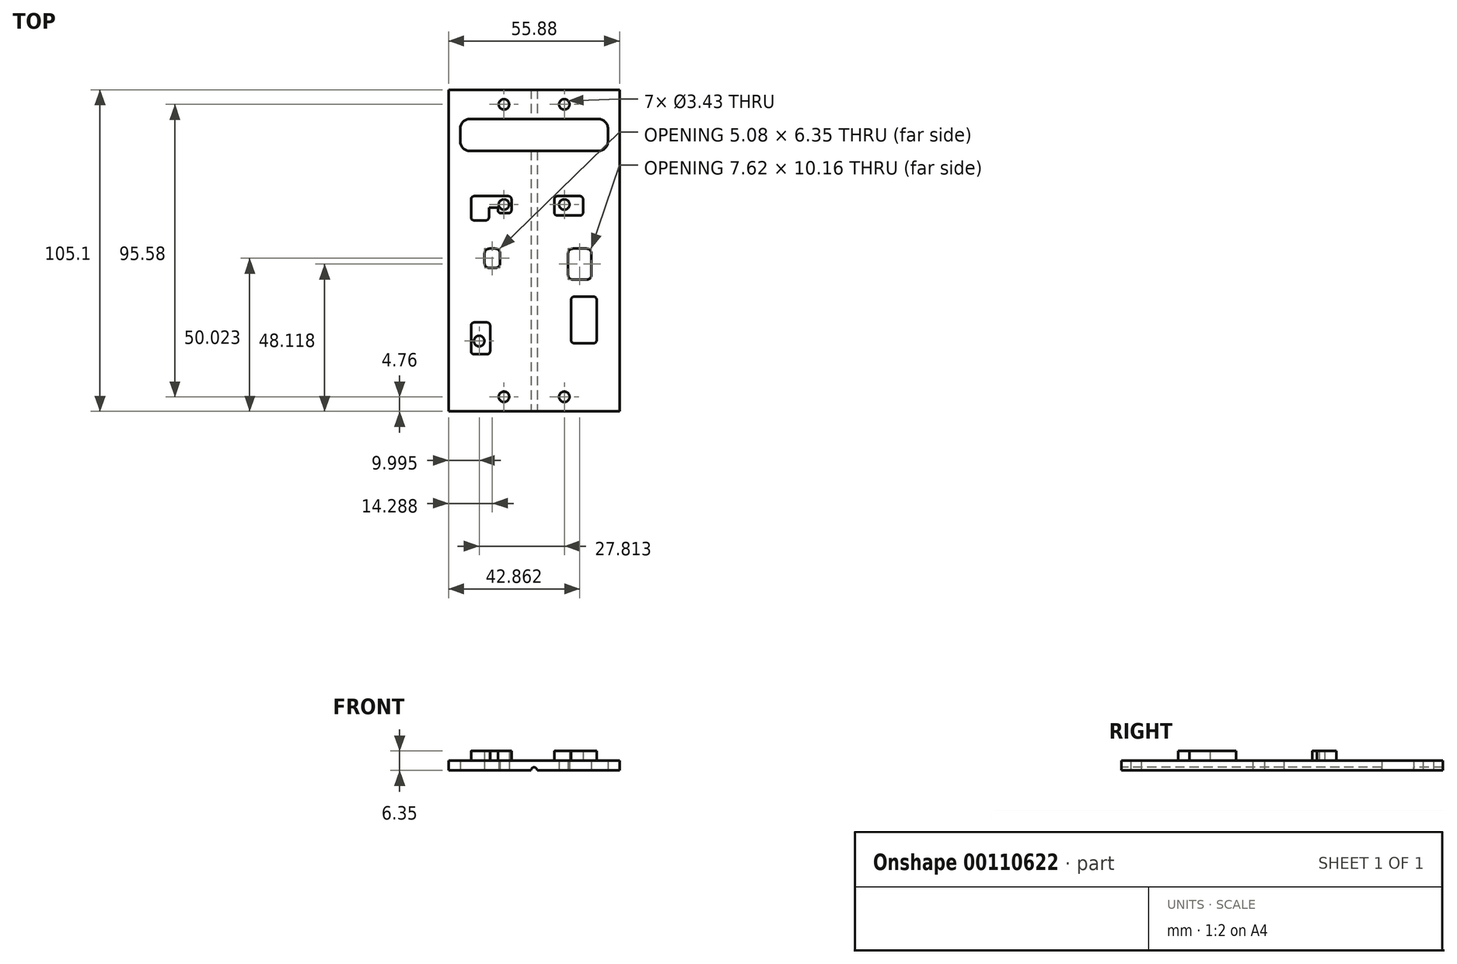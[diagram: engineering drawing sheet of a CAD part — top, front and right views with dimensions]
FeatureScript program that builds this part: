
annotation { "Feature Type Name" : "Feature", "Feature Type Description" : "" }
export const myFeature = defineFeature(function(context is Context, id is Id, definition is map)
    precondition{}
    {
        {
            var Q0;
            Q0=qCreatedBy(makeId("Top.planeOp"),FACE);
            var sketch = newSketch(context, id + "F0", { "sketchPlane" : qUnion([Q0])});
            skLineSegment(sketch, "E0.rect.bottom", {"start": v(27.94, 52.55) * mm, "end": v(-27.94, 52.55) * mm});
            skLineSegment(sketch, "E0.rect.top", {"start": v(27.94, -52.55) * mm, "end": v(-27.94, -52.55) * mm});
            skLineSegment(sketch, "E0.rect.left", {"start": v(27.94, 52.55) * mm, "end": v(27.94, -52.55) * mm});
            skLineSegment(sketch, "E0.rect.right", {"start": v(-27.94, 52.55) * mm, "end": v(-27.94, -52.55) * mm});
            skPoint(sketch, "E0.rect.middle", {"position": v(0, 0) * mm});
            skLineSegment(sketch, "E1.rect.bottom", {"start": v(24.13, 43.03) * mm, "end": v(-24.13, 43.03) * mm});
            skLineSegment(sketch, "E1.rect.top", {"start": v(24.13, 32.54) * mm, "end": v(-24.13, 32.54) * mm});
            skLineSegment(sketch, "E1.rect.left", {"start": v(24.13, 43.03) * mm, "end": v(24.13, 32.54) * mm});
            skLineSegment(sketch, "E1.rect.right", {"start": v(-24.13, 43.03) * mm, "end": v(-24.13, 32.54) * mm});
            skPoint(sketch, "E1.rect.middle", {"position": v(0, 37.78) * mm});
            skCircle(sketch, "E2", {"center": v(-9.87, 15.06) * mm, "radius": 1.71 * mm});
            skCircle(sketch, "E3", {"center": v(9.87, 15.06) * mm, "radius": 1.71 * mm});
            skLineSegment(sketch, "E4", {"start": v(-12.7, 29.36) * mm, "end": v(12.7, 29.36) * mm, "construction": true});
            skPoint(sketch, "E5", {"position": v(0, 29.36) * mm});
            skCircle(sketch, "E6", {"center": v(-9.87, 47.8) * mm, "radius": 1.71 * mm});
            skCircle(sketch, "E7", {"center": v(9.87, 47.8) * mm, "radius": 1.71 * mm});
            skLineSegment(sketch, "E8", {"start": v(0, 43.03) * mm, "end": v(0, 52.55) * mm, "construction": true});
            skPoint(sketch, "E9", {"position": v(0, 47.8) * mm});
            skCircle(sketch, "E10", {"center": v(-17.95, -29.57) * mm, "radius": 1.71 * mm});
            skLineSegment(sketch, "E11", {"start": v(-9.87, 15.06) * mm, "end": v(9.87, 15.06) * mm, "construction": true});
            skPoint(sketch, "E12", {"position": v(0, 15.06) * mm});
            skLineSegment(sketch, "E13", {"start": v(-27.94, -43.03) * mm, "end": v(27.94, -43.03) * mm, "construction": true});
            skCircle(sketch, "E14", {"center": v(-9.87, -47.8) * mm, "radius": 1.71 * mm});
            skCircle(sketch, "E15", {"center": v(9.87, -47.8) * mm, "radius": 1.71 * mm});
            skLineSegment(sketch, "E16", {"start": v(-9.87, -43.03) * mm, "end": v(-9.87, -52.55) * mm, "construction": true});
            skSolve(sketch);
        }
        {
            var Q0;
            Q0=qSketchRegion(id+"F0",true);
            extrude(context, id + "F1", {"entities" : qUnion([Q0]), "depth" : 3.17 * mm});
        }
        {
            var Q0;
            Q0=makeQuery(id+"F1.opExtrude","SWEPT_FACE",FACE,{"disambiguationData":[OSD([sQuery(id+"F0.wireOp",EDGE,"E0.rect.top")])]});
            var sketch = newSketch(context, id + "F2", { "sketchPlane" : qUnion([Q0])});
            skCircle(sketch, "E17", {"center": v(0, 0) * mm, "radius": 1.02 * mm});
            skSolve(sketch);
        }
        {
            var Q0;
            Q0=qSketchRegion(id+"F2",true);
            extrude(context, id + "F3", {"entities" : qUnion([Q0]), "operationType" : NewBodyOperationType.REMOVE, "endBound" : BoundingType.THROUGH_ALL, "oppositeDirection" : true, "depth" : 25.4 * mm});
        }
        {
            var Q0;
            Q0=makeQuery(id+"F1.opExtrude","CAP_FACE",FACE,{"disambiguationData":[OSD([sQuery(id+"F0.wireOp",EDGE,"E0.rect.bottom"),sQuery(id+"F0.wireOp",EDGE,"E0.rect.top"),sQuery(id+"F0.wireOp",EDGE,"E0.rect.left"),sQuery(id+"F0.wireOp",EDGE,"E0.rect.right"),sQuery(id+"F0.wireOp",EDGE,"E1.rect.bottom"),sQuery(id+"F0.wireOp",EDGE,"E1.rect.top"),sQuery(id+"F0.wireOp",EDGE,"E1.rect.left"),sQuery(id+"F0.wireOp",EDGE,"E1.rect.right"),sQuery(id+"F0.wireOp",EDGE,"E2"),sQuery(id+"F0.wireOp",EDGE,"E3"),sQuery(id+"F0.wireOp",EDGE,"E6"),sQuery(id+"F0.wireOp",EDGE,"E7"),sQuery(id+"F0.wireOp",EDGE,"E10"),sQuery(id+"F0.wireOp",EDGE,"a1c96030-42fa-4948-bc88-0ccc6f73de77")])],"isStart":false});
            var sketch = newSketch(context, id + "F4", { "sketchPlane" : qUnion([Q0])});
            skCircle(sketch, "E18", {"center": v(-17.95, -29.57) * mm, "radius": 1.71 * mm});
            skCircle(sketch, "E19", {"center": v(-9.87, 15.06) * mm, "radius": 1.71 * mm});
            skCircle(sketch, "E20", {"center": v(9.87, 15.06) * mm, "radius": 1.71 * mm});
            skLineSegment(sketch, "E21.bottom", {"start": v(20.45, 17.8) * mm, "end": v(-20.6, 17.8) * mm, "construction": true});
            skLineSegment(sketch, "E21.top", {"start": v(20.45, -33.9) * mm, "end": v(-20.6, -33.9) * mm, "construction": true});
            skLineSegment(sketch, "E21.left", {"start": v(20.45, 17.8) * mm, "end": v(20.45, -33.9) * mm, "construction": true});
            skLineSegment(sketch, "E21.right", {"start": v(-20.6, 17.8) * mm, "end": v(-20.6, -33.9) * mm, "construction": true});
            skLineSegment(sketch, "E22.bottom", {"start": v(-20.6, 17.8) * mm, "end": v(-7.4, 17.8) * mm});
            skLineSegment(sketch, "E22.left", {"start": v(-20.6, 17.8) * mm, "end": v(-20.6, 14.8) * mm});
            skLineSegment(sketch, "E22.right", {"start": v(-7.4, 17.8) * mm, "end": v(-7.4, 13.98) * mm});
            skLineSegment(sketch, "E23", {"start": v(-11.84, 13.98) * mm, "end": v(-14.76, 13.98) * mm});
            skLineSegment(sketch, "E24", {"start": v(-14.76, 13.98) * mm, "end": v(-14.76, 9.87) * mm});
            skLineSegment(sketch, "E25", {"start": v(-14.76, 9.87) * mm, "end": v(-20.6, 9.87) * mm});
            skLineSegment(sketch, "E26", {"start": v(-20.6, 9.87) * mm, "end": v(-20.6, 14.8) * mm});
            skLineSegment(sketch, "E27", {"start": v(-7.4, 13.98) * mm, "end": v(-7.4, 12.2) * mm});
            skLineSegment(sketch, "E28", {"start": v(-7.4, 12.2) * mm, "end": v(-11.84, 12.2) * mm});
            skLineSegment(sketch, "E29", {"start": v(-11.84, 12.2) * mm, "end": v(-11.84, 13.98) * mm});
            skLineSegment(sketch, "E30.bottom", {"start": v(16, 17.8) * mm, "end": v(6.63, 17.8) * mm});
            skLineSegment(sketch, "E30.top", {"start": v(16, 11.44) * mm, "end": v(6.63, 11.44) * mm});
            skLineSegment(sketch, "E30.left", {"start": v(16, 17.8) * mm, "end": v(16, 11.44) * mm});
            skLineSegment(sketch, "E30.right", {"start": v(6.63, 17.8) * mm, "end": v(6.63, 11.44) * mm});
            skLineSegment(sketch, "E31.bottom", {"start": v(-20.6, -33.9) * mm, "end": v(-14.38, -33.9) * mm});
            skLineSegment(sketch, "E31.top", {"start": v(-20.6, -23.48) * mm, "end": v(-14.38, -23.48) * mm});
            skLineSegment(sketch, "E31.left", {"start": v(-20.6, -33.9) * mm, "end": v(-20.6, -23.48) * mm});
            skLineSegment(sketch, "E31.right", {"start": v(-14.38, -33.9) * mm, "end": v(-14.38, -23.48) * mm});
            skLineSegment(sketch, "E32.bottom", {"start": v(20.45, -15.05) * mm, "end": v(12.1, -15.05) * mm});
            skLineSegment(sketch, "E32.top", {"start": v(20.45, -30.29) * mm, "end": v(12.1, -30.29) * mm});
            skLineSegment(sketch, "E32.left", {"start": v(20.45, -15.05) * mm, "end": v(20.45, -30.29) * mm});
            skLineSegment(sketch, "E32.right", {"start": v(12.1, -15.05) * mm, "end": v(12.1, -30.29) * mm});
            skSolve(sketch);
        }
        {
            var Q0;
            Q0=qSketchRegion(id+"F4",true);
            extrude(context, id + "F5", {"entities" : qUnion([Q0]), "operationType" : NewBodyOperationType.ADD, "depth" : 3.17 * mm});
        }
        {
            var Q0;
            {var subQ0=sQuery(id+"F0.wireOp",EDGE,"E1.rect.bottom");var subQ1=sQuery(id+"F0.wireOp",EDGE,"E0.rect.left");var subQ2=sQuery(id+"F0.wireOp",EDGE,"E0.rect.top");var subQ3=sQuery(id+"F0.wireOp",EDGE,"E0.rect.bottom");var subQ4=sQuery(id+"F0.wireOp",EDGE,"E1.rect.top");var subQ5=sQuery(id+"F0.wireOp",EDGE,"E1.rect.left");var subQ6=sQuery(id+"F0.wireOp",EDGE,"E3");var subQ7=sQuery(id+"F0.wireOp",EDGE,"E7");var subQ8=sQuery(id+"F0.wireOp",EDGE,"a1c96030-42fa-4948-bc88-0ccc6f73de77");Q0=makeQuery(id+"F3.boolean.opBoolean","SPLIT",FACE,{"disambiguationData":[TD([makeQuery(id+"F1.opExtrude","SWEPT_FACE",FACE,{"disambiguationData":[OSD([subQ1])]})])],"derivedFrom":makeQuery(id+"F1.opExtrude","CAP_FACE",FACE,{"disambiguationData":[OSD([subQ3,subQ2,subQ1,sQuery(id+"F0.wireOp",EDGE,"E0.rect.right"),subQ0,subQ4,subQ5,sQuery(id+"F0.wireOp",EDGE,"E1.rect.right"),sQuery(id+"F0.wireOp",EDGE,"E2"),subQ6,sQuery(id+"F0.wireOp",EDGE,"E6"),subQ7,sQuery(id+"F0.wireOp",EDGE,"E10"),subQ8])],"isStart":true})});}
            var sketch = newSketch(context, id + "F6", { "sketchPlane" : qUnion([Q0])});
            skLineSegment(sketch, "E33.rect.bottom", {"start": v(18.73, 9.51) * mm, "end": v(11.11, 9.51) * mm});
            skLineSegment(sketch, "E33.rect.top", {"start": v(18.73, -0.65) * mm, "end": v(11.11, -0.65) * mm});
            skLineSegment(sketch, "E33.rect.left", {"start": v(11.11, 9.51) * mm, "end": v(11.11, -0.65) * mm});
            skLineSegment(sketch, "E33.rect.right", {"start": v(18.73, 9.51) * mm, "end": v(18.73, -0.65) * mm});
            skPoint(sketch, "E33.rect.middle", {"position": v(14.92, 4.43) * mm});
            skLineSegment(sketch, "E34.rect.bottom", {"start": v(-11.11, 5.7) * mm, "end": v(-16.2, 5.7) * mm});
            skLineSegment(sketch, "E34.rect.top", {"start": v(-11.11, -0.65) * mm, "end": v(-16.2, -0.65) * mm});
            skLineSegment(sketch, "E34.rect.left", {"start": v(-16.2, 5.7) * mm, "end": v(-16.2, -0.65) * mm});
            skLineSegment(sketch, "E34.rect.right", {"start": v(-11.11, 5.7) * mm, "end": v(-11.11, -0.65) * mm});
            skPoint(sketch, "E34.rect.middle", {"position": v(-13.65, 2.53) * mm});
            skSolve(sketch);
        }
        {
            var Q0;
            Q0=qSketchRegion(id+"F6",true);
            extrude(context, id + "F7", {"entities" : qUnion([Q0]), "operationType" : NewBodyOperationType.REMOVE, "oppositeDirection" : true, "depth" : 25.4 * mm});
        }
        {
            var Q0;
            Q0=makeQuery(id+"F7.boolean.opBoolean","COPY",EDGE,{"derivedFrom":makeQuery(id+"F7.opExtrude","SWEPT_EDGE",EDGE,{"disambiguationData":[OSD([sQuery(id+"F6.wireOp",EDGE,"E34.rect.top"),sQuery(id+"F6.wireOp",EDGE,"E34.rect.left")])]})});
            var Q1;
            Q1=makeQuery(id+"F7.boolean.opBoolean","COPY",EDGE,{"derivedFrom":makeQuery(id+"F7.opExtrude","SWEPT_EDGE",EDGE,{"disambiguationData":[OSD([sQuery(id+"F6.wireOp",EDGE,"E33.rect.top"),sQuery(id+"F6.wireOp",EDGE,"E33.rect.left")])]})});
            var Q2;
            Q2=makeQuery(id+"F7.boolean.opBoolean","COPY",EDGE,{"derivedFrom":makeQuery(id+"F7.opExtrude","SWEPT_EDGE",EDGE,{"disambiguationData":[OSD([sQuery(id+"F6.wireOp",EDGE,"E33.rect.top"),sQuery(id+"F6.wireOp",EDGE,"E33.rect.right")])]})});
            var Q3;
            Q3=makeQuery(id+"F7.boolean.opBoolean","COPY",EDGE,{"derivedFrom":makeQuery(id+"F7.opExtrude","SWEPT_EDGE",EDGE,{"disambiguationData":[OSD([sQuery(id+"F6.wireOp",EDGE,"E33.rect.bottom"),sQuery(id+"F6.wireOp",EDGE,"E33.rect.right")])]})});
            var Q4;
            Q4=makeQuery(id+"F7.boolean.opBoolean","COPY",EDGE,{"derivedFrom":makeQuery(id+"F7.opExtrude","SWEPT_EDGE",EDGE,{"disambiguationData":[OSD([sQuery(id+"F6.wireOp",EDGE,"E33.rect.bottom"),sQuery(id+"F6.wireOp",EDGE,"E33.rect.left")])]})});
            var Q5;
            Q5=makeQuery(id+"F7.boolean.opBoolean","COPY",EDGE,{"derivedFrom":makeQuery(id+"F7.opExtrude","SWEPT_EDGE",EDGE,{"disambiguationData":[OSD([sQuery(id+"F6.wireOp",EDGE,"E34.rect.bottom"),sQuery(id+"F6.wireOp",EDGE,"E34.rect.left")])]})});
            var Q6;
            Q6=makeQuery(id+"F7.boolean.opBoolean","COPY",EDGE,{"derivedFrom":makeQuery(id+"F7.opExtrude","SWEPT_EDGE",EDGE,{"disambiguationData":[OSD([sQuery(id+"F6.wireOp",EDGE,"E34.rect.bottom"),sQuery(id+"F6.wireOp",EDGE,"E34.rect.right")])]})});
            var Q7;
            Q7=makeQuery(id+"F7.boolean.opBoolean","COPY",EDGE,{"derivedFrom":makeQuery(id+"F7.opExtrude","SWEPT_EDGE",EDGE,{"disambiguationData":[OSD([sQuery(id+"F6.wireOp",EDGE,"E34.rect.top"),sQuery(id+"F6.wireOp",EDGE,"E34.rect.right")])]})});
            var Q8;
            Q8=makeQuery(id+"F5.opExtrude","SWEPT_EDGE",EDGE,{"disambiguationData":[OSD([sQuery(id+"F4.wireOp",EDGE,"dba2aca7-0b01-4150-9072-14bcdbd6973b.rect.top"),sQuery(id+"F4.wireOp",EDGE,"dba2aca7-0b01-4150-9072-14bcdbd6973b.rect.right")])]});
            var Q9;
            Q9=makeQuery(id+"F5.opExtrude","SWEPT_EDGE",EDGE,{"disambiguationData":[OSD([sQuery(id+"F4.wireOp",EDGE,"dba2aca7-0b01-4150-9072-14bcdbd6973b.rect.bottom"),sQuery(id+"F4.wireOp",EDGE,"dba2aca7-0b01-4150-9072-14bcdbd6973b.rect.right")])]});
            var Q10;
            Q10=makeQuery(id+"F5.opExtrude","SWEPT_EDGE",EDGE,{"disambiguationData":[OSD([sQuery(id+"F4.wireOp",EDGE,"dba2aca7-0b01-4150-9072-14bcdbd6973b.rect.top"),sQuery(id+"F4.wireOp",EDGE,"dba2aca7-0b01-4150-9072-14bcdbd6973b.rect.left")])]});
            var Q11;
            Q11=makeQuery(id+"F5.opExtrude","SWEPT_EDGE",EDGE,{"disambiguationData":[OSD([sQuery(id+"F4.wireOp",EDGE,"dba2aca7-0b01-4150-9072-14bcdbd6973b.rect.bottom"),sQuery(id+"F4.wireOp",EDGE,"dba2aca7-0b01-4150-9072-14bcdbd6973b.rect.left")])]});
            fillet(context, id + "F8", {"entities" : qUnion([Q0, Q1, Q2, Q3, Q4, Q5, Q6, Q7, Q8, Q9, Q10, Q11]), "radius" : 1.6 * mm, "tangentPropagation" : true, "allowEdgeOverflow" : false});
        }
        {
            var Q0;
            Q0=makeQuery(id+"F1.opExtrude","SWEPT_EDGE",EDGE,{"disambiguationData":[OSD([sQuery(id+"F0.wireOp",EDGE,"E1.rect.top"),sQuery(id+"F0.wireOp",EDGE,"E1.rect.right")])]});
            var Q1;
            Q1=makeQuery(id+"F1.opExtrude","SWEPT_EDGE",EDGE,{"disambiguationData":[OSD([sQuery(id+"F0.wireOp",EDGE,"E1.rect.top"),sQuery(id+"F0.wireOp",EDGE,"E1.rect.left")])]});
            var Q2;
            Q2=makeQuery(id+"F1.opExtrude","SWEPT_EDGE",EDGE,{"disambiguationData":[OSD([sQuery(id+"F0.wireOp",EDGE,"E1.rect.bottom"),sQuery(id+"F0.wireOp",EDGE,"E1.rect.left")])]});
            var Q3;
            Q3=makeQuery(id+"F1.opExtrude","SWEPT_EDGE",EDGE,{"disambiguationData":[OSD([sQuery(id+"F0.wireOp",EDGE,"E1.rect.bottom"),sQuery(id+"F0.wireOp",EDGE,"E1.rect.right")])]});
            fillet(context, id + "F9", {"entities" : qUnion([Q0, Q1, Q2, Q3]), "radius" : 3.17 * mm, "tangentPropagation" : true, "allowEdgeOverflow" : false});
        }
        {
            var Q0;
            Q0=makeQuery(id+"F5.opExtrude","SWEPT_EDGE",EDGE,{"disambiguationData":[OSD([sQuery(id+"F4.wireOp",EDGE,"E22.bottom"),sQuery(id+"F4.wireOp",EDGE,"E22.right")])]});
            var Q1;
            Q1=makeQuery(id+"F5.opExtrude","SWEPT_EDGE",EDGE,{"disambiguationData":[OSD([sQuery(id+"F4.wireOp",EDGE,"E30.bottom"),sQuery(id+"F4.wireOp",EDGE,"E30.right")])]});
            var Q2;
            Q2=makeQuery(id+"F5.opExtrude","SWEPT_EDGE",EDGE,{"disambiguationData":[OSD([sQuery(id+"F4.wireOp",EDGE,"E30.bottom"),sQuery(id+"F4.wireOp",EDGE,"E30.left")])]});
            var Q3;
            Q3=makeQuery(id+"F5.opExtrude","SWEPT_EDGE",EDGE,{"disambiguationData":[OSD([sQuery(id+"F4.wireOp",EDGE,"E32.bottom"),sQuery(id+"F4.wireOp",EDGE,"E32.left")])]});
            var Q4;
            Q4=makeQuery(id+"F5.opExtrude","SWEPT_EDGE",EDGE,{"disambiguationData":[OSD([sQuery(id+"F4.wireOp",EDGE,"E32.bottom"),sQuery(id+"F4.wireOp",EDGE,"E32.right")])]});
            var Q5;
            Q5=makeQuery(id+"F5.opExtrude","SWEPT_EDGE",EDGE,{"disambiguationData":[OSD([sQuery(id+"F4.wireOp",EDGE,"E32.top"),sQuery(id+"F4.wireOp",EDGE,"E32.left")])]});
            var Q6;
            Q6=makeQuery(id+"F5.opExtrude","SWEPT_EDGE",EDGE,{"disambiguationData":[OSD([sQuery(id+"F4.wireOp",EDGE,"E32.top"),sQuery(id+"F4.wireOp",EDGE,"E32.right")])]});
            var Q7;
            Q7=makeQuery(id+"F5.opExtrude","SWEPT_EDGE",EDGE,{"disambiguationData":[OSD([sQuery(id+"F4.wireOp",EDGE,"E31.bottom"),sQuery(id+"F4.wireOp",EDGE,"E31.right")])]});
            var Q8;
            Q8=makeQuery(id+"F5.opExtrude","SWEPT_EDGE",EDGE,{"disambiguationData":[OSD([sQuery(id+"F4.wireOp",EDGE,"E31.bottom"),sQuery(id+"F4.wireOp",EDGE,"E31.left")])]});
            var Q9;
            Q9=makeQuery(id+"F5.opExtrude","SWEPT_EDGE",EDGE,{"disambiguationData":[OSD([sQuery(id+"F4.wireOp",EDGE,"E31.top"),sQuery(id+"F4.wireOp",EDGE,"E31.right")])]});
            var Q10;
            Q10=makeQuery(id+"F5.opExtrude","SWEPT_EDGE",EDGE,{"disambiguationData":[OSD([sQuery(id+"F4.wireOp",EDGE,"E31.top"),sQuery(id+"F4.wireOp",EDGE,"E31.left")])]});
            var Q11;
            Q11=makeQuery(id+"F5.opExtrude","SWEPT_EDGE",EDGE,{"disambiguationData":[OSD([sQuery(id+"F4.wireOp",EDGE,"E30.top"),sQuery(id+"F4.wireOp",EDGE,"E30.right")])]});
            var Q12;
            Q12=makeQuery(id+"F5.opExtrude","SWEPT_EDGE",EDGE,{"disambiguationData":[OSD([sQuery(id+"F4.wireOp",EDGE,"E30.top"),sQuery(id+"F4.wireOp",EDGE,"E30.left")])]});
            var Q13;
            Q13=makeQuery(id+"F5.opExtrude","SWEPT_EDGE",EDGE,{"disambiguationData":[OSD([sQuery(id+"F4.wireOp",EDGE,"E22.bottom"),sQuery(id+"F4.wireOp",EDGE,"E22.left")])]});
            var Q14;
            Q14=makeQuery(id+"F5.opExtrude","SWEPT_EDGE",EDGE,{"disambiguationData":[OSD([sQuery(id+"F4.wireOp",EDGE,"E25"),sQuery(id+"F4.wireOp",EDGE,"E26")])]});
            var Q15;
            Q15=makeQuery(id+"F5.opExtrude","SWEPT_EDGE",EDGE,{"disambiguationData":[OSD([sQuery(id+"F4.wireOp",EDGE,"E24"),sQuery(id+"F4.wireOp",EDGE,"E25")])]});
            var Q16;
            Q16=makeQuery(id+"F5.opExtrude","SWEPT_EDGE",EDGE,{"disambiguationData":[OSD([sQuery(id+"F4.wireOp",EDGE,"E27"),sQuery(id+"F4.wireOp",EDGE,"E28")])]});
            var Q17;
            Q17=makeQuery(id+"F5.opExtrude","SWEPT_EDGE",EDGE,{"disambiguationData":[OSD([sQuery(id+"F4.wireOp",EDGE,"E28"),sQuery(id+"F4.wireOp",EDGE,"E29")])]});
            var Q18;
            Q18=makeQuery(id+"F5.opExtrude","CAP_EDGE",EDGE,{"disambiguationData":[OSD([sQuery(id+"F4.wireOp",EDGE,"E31.right")])],"isStart":true});
            var Q19;
            Q19=makeQuery(id+"F5.opExtrude","CAP_EDGE",EDGE,{"disambiguationData":[OSD([sQuery(id+"F4.wireOp",EDGE,"E32.left")])],"isStart":true});
            var Q20;
            Q20=makeQuery(id+"F5.opExtrude","CAP_EDGE",EDGE,{"disambiguationData":[OSD([sQuery(id+"F4.wireOp",EDGE,"E30.left")])],"isStart":true});
            var Q21;
            Q21=makeQuery(id+"F5.opExtrude","CAP_EDGE",EDGE,{"disambiguationData":[OSD([sQuery(id+"F4.wireOp",EDGE,"E22.right"),sQuery(id+"F4.wireOp",EDGE,"E27")])],"isStart":true});
            fillet(context, id + "F10", {"entities" : qUnion([Q0, Q1, Q2, Q3, Q4, Q5, Q6, Q7, Q8, Q9, Q10, Q11, Q12, Q13, Q14, Q15, Q16, Q17, Q18, Q19, Q20, Q21]), "radius" : 1.02 * mm, "tangentPropagation" : true, "allowEdgeOverflow" : false});
        }
    });
